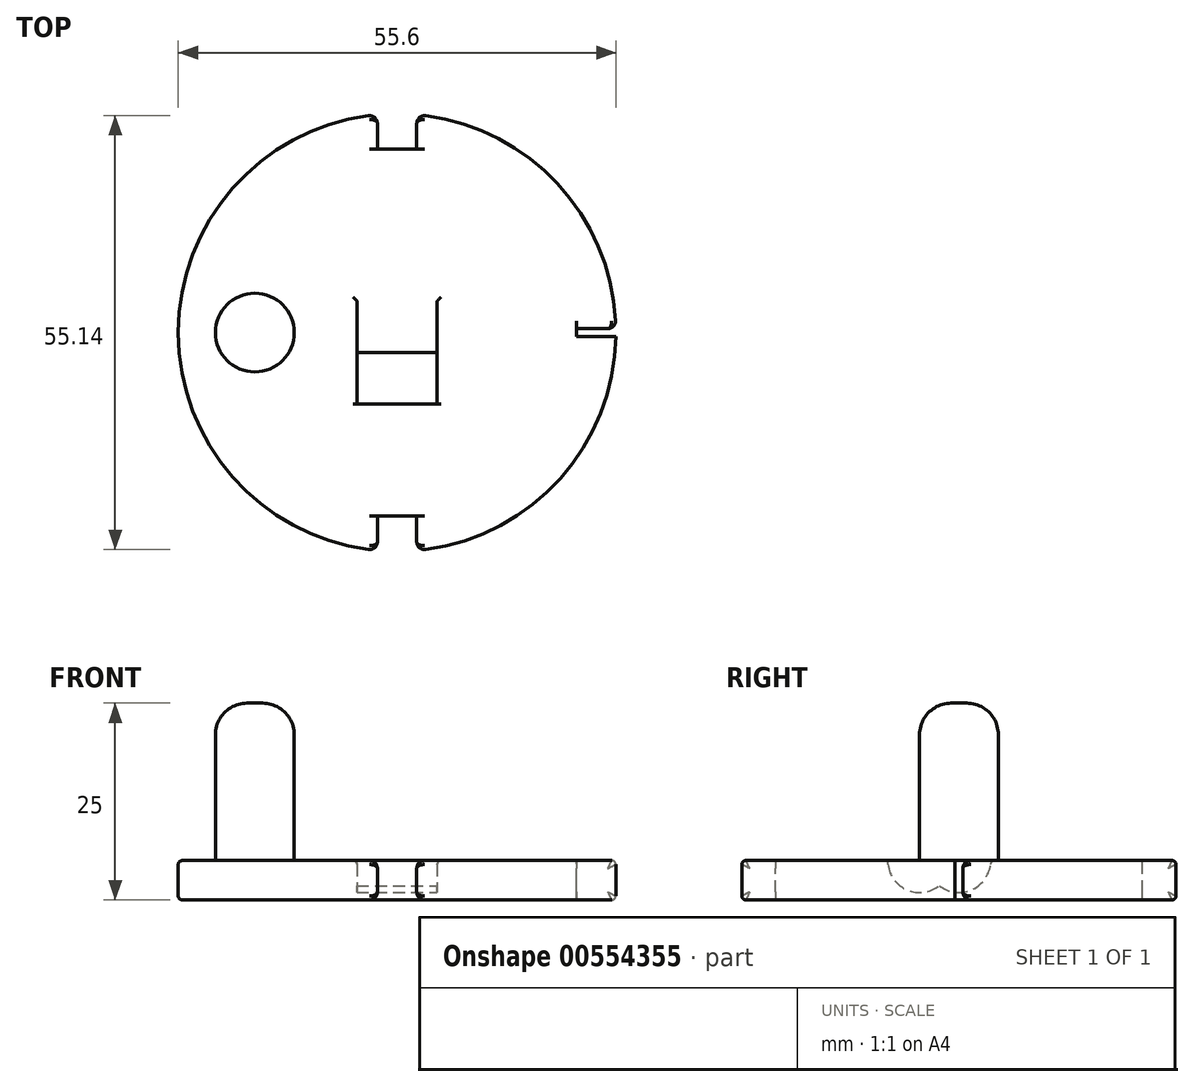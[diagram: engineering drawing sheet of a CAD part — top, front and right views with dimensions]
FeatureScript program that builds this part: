
annotation { "Feature Type Name" : "Feature", "Feature Type Description" : "" }
export const myFeature = defineFeature(function(context is Context, id is Id, definition is map)
    precondition{}
    {
        {
            var Q0;
            Q0=qCreatedBy(makeId("Top.planeOp"),FACE);
            var sketch = newSketch(context, id + "F0", { "sketchPlane" : qUnion([Q0])});
            skCircle(sketch, "E0", {"center": v(0, 0) * mm, "radius": 27.8 * mm});
            skSolve(sketch);
        }
        {
            var Q0;
            Q0=qSketchRegion(id+"F0",true);
            extrude(context, id + "F1", {"entities" : qUnion([Q0]), "depth" : 5 * mm, "offsetDistance" : 25 * mm});
        }
        {
            var Q0;
            Q0=makeQuery(id+"F1.opExtrude","CAP_FACE",FACE,{"disambiguationData":[OSD([sQuery(id+"F0.wireOp",EDGE,"E0")])],"isStart":false});
            var Q1;
            Q1=makeQuery(id+"F1.opExtrude","CAP_FACE",FACE,{"disambiguationData":[OSD([sQuery(id+"F0.wireOp",EDGE,"E0")])],"isStart":true});
            fillet(context, id + "F2", {"entities" : qUnion([Q0, Q1]), "radius" : 0.5 * mm, "tangentPropagation" : true, "allowEdgeOverflow" : false});
        }
        {
            var Q0;
            Q0=makeQuery(id+"F1.opExtrude","CAP_FACE",FACE,{"disambiguationData":[OSD([sQuery(id+"F0.wireOp",EDGE,"E0")])],"isStart":false});
            var sketch = newSketch(context, id + "F3", { "sketchPlane" : qUnion([Q0])});
            skLineSegment(sketch, "E1.bottom", {"start": v(-2.5, 28.3) * mm, "end": v(2.5, 28.3) * mm});
            skLineSegment(sketch, "E1.top", {"start": v(-2.5, 23.3) * mm, "end": v(2.5, 23.3) * mm});
            skLineSegment(sketch, "E1.left", {"start": v(-2.5, 28.3) * mm, "end": v(-2.5, 23.3) * mm});
            skLineSegment(sketch, "E1.right", {"start": v(2.5, 28.3) * mm, "end": v(2.5, 23.3) * mm});
            skPoint(sketch, "E1.middle", {"position": v(0, 25.8) * mm});
            skLineSegment(sketch, "E2.MirrorCS", {"start": v(-2.5, -23.3) * mm, "end": v(2.5, -23.3) * mm});
            skLineSegment(sketch, "E3.MirrorCS", {"start": v(-2.5, -28.3) * mm, "end": v(2.5, -28.3) * mm});
            skLineSegment(sketch, "E4.MirrorCS", {"start": v(-2.5, -28.3) * mm, "end": v(-2.5, -23.3) * mm});
            skPoint(sketch, "E5.MirrorP", {"position": v(0, -25.8) * mm});
            skLineSegment(sketch, "E6.MirrorCS", {"start": v(2.5, -28.3) * mm, "end": v(2.5, -23.3) * mm});
            skSolve(sketch);
        }
        {
            var Q0;
            Q0=qSketchRegion(id+"F3",true);
            extrude(context, id + "F4", {"entities" : qUnion([Q0]), "operationType" : NewBodyOperationType.REMOVE, "endBound" : BoundingType.THROUGH_ALL, "oppositeDirection" : true, "depth" : 25 * mm, "offsetDistance" : 25 * mm});
        }
        {
            var Q0;
            Q0=makeQuery(id+"F4.boolean.opBoolean","INTERSECT",EDGE,{"derivedFrom":[makeQuery(id+"F1.opExtrude","SWEPT_FACE",FACE,{"disambiguationData":[OSD([sQuery(id+"F0.wireOp",EDGE,"E0")])]}),makeQuery(id+"F4.opExtrude","SWEPT_FACE",FACE,{"disambiguationData":[OSD([sQuery(id+"F3.wireOp",EDGE,"E4.MirrorCS")])]})]});
            var Q1;
            Q1=makeQuery(id+"F4.boolean.opBoolean","INTERSECT",EDGE,{"derivedFrom":[makeQuery(id+"F1.opExtrude","SWEPT_FACE",FACE,{"disambiguationData":[OSD([sQuery(id+"F0.wireOp",EDGE,"E0")])]}),makeQuery(id+"F4.opExtrude","SWEPT_FACE",FACE,{"disambiguationData":[OSD([sQuery(id+"F3.wireOp",EDGE,"E6.MirrorCS")])]})]});
            var Q2;
            Q2=makeQuery(id+"F4.boolean.opBoolean","INTERSECT",EDGE,{"derivedFrom":[makeQuery(id+"F1.opExtrude","SWEPT_FACE",FACE,{"disambiguationData":[OSD([sQuery(id+"F0.wireOp",EDGE,"E0")])]}),makeQuery(id+"F4.opExtrude","SWEPT_FACE",FACE,{"disambiguationData":[OSD([sQuery(id+"F3.wireOp",EDGE,"E1.left")])]})]});
            var Q3;
            Q3=makeQuery(id+"F4.boolean.opBoolean","INTERSECT",EDGE,{"derivedFrom":[makeQuery(id+"F1.opExtrude","SWEPT_FACE",FACE,{"disambiguationData":[OSD([sQuery(id+"F0.wireOp",EDGE,"E0")])]}),makeQuery(id+"F4.opExtrude","SWEPT_FACE",FACE,{"disambiguationData":[OSD([sQuery(id+"F3.wireOp",EDGE,"E1.right")])]})]});
            fillet(context, id + "F5", {"entities" : qUnion([Q0, Q1, Q2, Q3]), "radius" : 1 * mm, "tangentPropagation" : true, "allowEdgeOverflow" : false});
        }
        {
            var Q0;
            Q0=makeQuery(id+"F1.opExtrude","CAP_FACE",FACE,{"disambiguationData":[OSD([sQuery(id+"F0.wireOp",EDGE,"E0")])],"isStart":false});
            var sketch = newSketch(context, id + "F6", { "sketchPlane" : qUnion([Q0])});
            skCircle(sketch, "E7", {"center": v(-18.07, 0) * mm, "radius": 5 * mm});
            skSolve(sketch);
        }
        {
            var Q0;
            Q0=qSketchRegion(id+"F6",true);
            extrude(context, id + "F7", {"entities" : qUnion([Q0]), "operationType" : NewBodyOperationType.ADD, "depth" : 20 * mm, "offsetDistance" : 25 * mm});
        }
        {
            var Q0;
            Q0=makeQuery(id+"F7.opExtrude","CAP_FACE",FACE,{"disambiguationData":[OSD([sQuery(id+"F6.wireOp",EDGE,"E7")])],"isStart":false});
            var Q1;
            Q1=makeQuery(id+"F7.opExtrude","CAP_EDGE",EDGE,{"disambiguationData":[OSD([sQuery(id+"F6.wireOp",EDGE,"E7")])],"isStart":true});
            fillet(context, id + "F8", {"entities" : qUnion([Q0, Q1]), "radius" : 4 * mm, "tangentPropagation" : true, "allowEdgeOverflow" : false});
        }
        {
            var Q0;
            Q0=makeQuery(id+"F1.opExtrude","CAP_FACE",FACE,{"disambiguationData":[OSD([sQuery(id+"F0.wireOp",EDGE,"E0")])],"isStart":false});
            var sketch = newSketch(context, id + "F9", { "sketchPlane" : qUnion([Q0])});
            skLineSegment(sketch, "E8.bottom", {"start": v(27.8, -0.5) * mm, "end": v(22.8, -0.5) * mm});
            skLineSegment(sketch, "E8.top", {"start": v(27.8, 0.5) * mm, "end": v(22.8, 0.5) * mm});
            skLineSegment(sketch, "E8.left", {"start": v(27.8, -0.5) * mm, "end": v(27.8, 0.5) * mm});
            skLineSegment(sketch, "E8.right", {"start": v(22.8, -0.5) * mm, "end": v(22.8, 0.5) * mm});
            skPoint(sketch, "E8.middle", {"position": v(25.3, 0) * mm});
            skPoint(sketch, "E8.middle.positionSnap0", {"position": v(27.3, 0) * mm});
            skPoint(sketch, "E8.centerSnap0", {"position": v(27.3, 0) * mm});
            skSolve(sketch);
        }
        {
            var Q0;
            {var subQ0=sQuery(id+"F9.wireOp",EDGE,"E8.right");Q0=makeQuery(id+"F9.imprint","IMPRINT",FACE,{"disambiguationData":[TD([[makeQuery(id+"F9.imprint","IMPRINT",EDGE,{"derivedFrom":subQ0}),-1.0]])]});}
            var Q1;
            Q1=qSketchRegion(id+"F9",true);
            extrude(context, id + "F10", {"entities" : qUnion([Q0, Q1]), "operationType" : NewBodyOperationType.REMOVE, "endBound" : BoundingType.THROUGH_ALL, "oppositeDirection" : true, "depth" : 25 * mm, "offsetDistance" : 25 * mm});
        }
        {
            var Q0;
            Q0=makeQuery(id+"F10.boolean.opBoolean","COPY",EDGE,{"derivedFrom":makeQuery(id+"F10.opExtrude","SWEPT_EDGE",EDGE,{"disambiguationData":[OSD([sQuery(id+"F9.wireOp",EDGE,"E8.top"),sQuery(id+"F9.wireOp",EDGE,"E8.left")])]})});
            var Q1;
            Q1=makeQuery(id+"F10.boolean.opBoolean","COPY",EDGE,{"derivedFrom":makeQuery(id+"F10.opExtrude","SWEPT_EDGE",EDGE,{"disambiguationData":[OSD([sQuery(id+"F9.wireOp",EDGE,"E8.bottom"),sQuery(id+"F9.wireOp",EDGE,"E8.left")])]})});
            fillet(context, id + "F11", {"entities" : qUnion([Q0, Q1]), "radius" : 1 * mm, "tangentPropagation" : true, "allowEdgeOverflow" : false});
        }
        {
            var Q0;
            Q0=qCreatedBy(makeId("Right.planeOp"),FACE);
            var sketch = newSketch(context, id + "F12", { "sketchPlane" : qUnion([Q0])});
            skCircle(sketch, "E9", {"center": v(0, 5) * mm, "radius": 4.05 * mm});
            skCircle(sketch, "E10", {"center": v(-5, 5) * mm, "radius": 4.05 * mm});
            skSolve(sketch);
        }
        {
            var Q0;
            Q0=qSketchRegion(id+"F12",true);
            extrude(context, id + "F13", {"entities" : qUnion([Q0]), "operationType" : NewBodyOperationType.REMOVE, "oppositeDirection" : true, "depth" : 5.1 * mm, "offsetDistance" : 25 * mm, "hasSecondDirection" : true, "secondDirectionOppositeDirection" : false, "secondDirectionDepth" : 5.1 * mm});
        }
        {
            var Q0;
            Q0=makeQuery(id+"F13.boolean.opBoolean","INTERSECT",EDGE,{"derivedFrom":[makeQuery(id+"F1.opExtrude","CAP_FACE",FACE,{"disambiguationData":[OSD([sQuery(id+"F0.wireOp",EDGE,"E0")])],"isStart":false}),makeQuery(id+"F13.opExtrude","CAP_FACE",FACE,{"disambiguationData":[OSD([sQuery(id+"F12.wireOp",EDGE,"E9")])],"isStart":true})]});
            var Q1;
            Q1=makeQuery(id+"F13.boolean.opBoolean","INTERSECT",EDGE,{"disambiguationData":[OD(0.0)],"derivedFrom":[makeQuery(id+"F1.opExtrude","CAP_FACE",FACE,{"disambiguationData":[OSD([sQuery(id+"F0.wireOp",EDGE,"E0")])],"isStart":false}),makeQuery(id+"F13.opExtrude","SWEPT_FACE",FACE,{"disambiguationData":[OSD([sQuery(id+"F12.wireOp",EDGE,"E9")])]})]});
            var Q2;
            Q2=makeQuery(id+"F13.boolean.opBoolean","INTERSECT",EDGE,{"disambiguationData":[OD(1.0)],"derivedFrom":[makeQuery(id+"F1.opExtrude","CAP_FACE",FACE,{"disambiguationData":[OSD([sQuery(id+"F0.wireOp",EDGE,"E0")])],"isStart":false}),makeQuery(id+"F13.opExtrude","SWEPT_FACE",FACE,{"disambiguationData":[OSD([sQuery(id+"F12.wireOp",EDGE,"E9")])]})]});
            var Q3;
            Q3=makeQuery(id+"F13.boolean.opBoolean","INTERSECT",EDGE,{"derivedFrom":[makeQuery(id+"F1.opExtrude","CAP_FACE",FACE,{"disambiguationData":[OSD([sQuery(id+"F0.wireOp",EDGE,"E0")])],"isStart":false}),makeQuery(id+"F13.opExtrude","CAP_FACE",FACE,{"disambiguationData":[OSD([sQuery(id+"F12.wireOp",EDGE,"E9")])],"isStart":false})]});
            fillet(context, id + "F14", {"entities" : qUnion([Q0, Q1, Q2, Q3]), "radius" : 0.5 * mm, "tangentPropagation" : true, "allowEdgeOverflow" : false});
        }
    });
